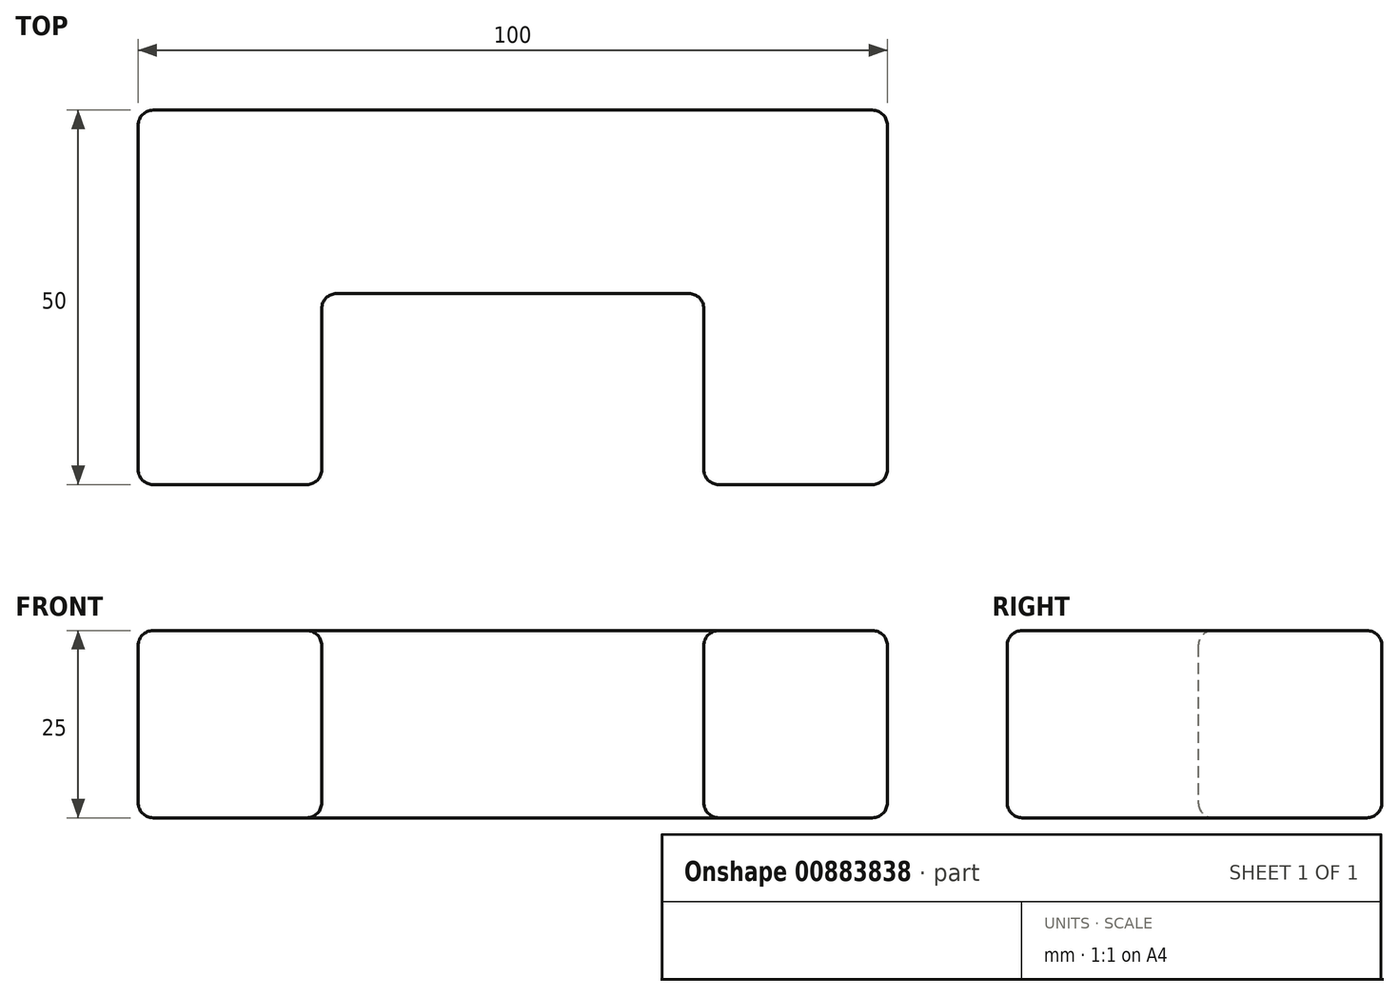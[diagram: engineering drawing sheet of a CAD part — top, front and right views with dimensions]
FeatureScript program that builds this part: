
annotation { "Feature Type Name" : "Feature", "Feature Type Description" : "" }
export const myFeature = defineFeature(function(context is Context, id is Id, definition is map)
    precondition{}
    {
        {
            var Q0;
            Q0=qCreatedBy(makeId("Top.planeOp"),FACE);
            var sketch = newSketch(context, id + "F0", { "sketchPlane" : qUnion([Q0])});
            skLineSegment(sketch, "E0", {"start": v(-50, 0) * mm, "end": v(-50, 50) * mm});
            skLineSegment(sketch, "E1", {"start": v(-50, 0) * mm, "end": v(-25.5, 0) * mm});
            skLineSegment(sketch, "E2", {"start": v(-25.5, 0) * mm, "end": v(-25.5, 25.5) * mm});
            skLineSegment(sketch, "E3.MirrorCS", {"start": v(25.5, 0) * mm, "end": v(25.5, 25.5) * mm});
            skLineSegment(sketch, "E4.MirrorCS", {"start": v(50, 0) * mm, "end": v(25.5, 0) * mm});
            skLineSegment(sketch, "E5.MirrorCS", {"start": v(50, 0) * mm, "end": v(50, 50) * mm});
            skLineSegment(sketch, "E6", {"start": v(-50, 50) * mm, "end": v(50, 50) * mm});
            skLineSegment(sketch, "E7", {"start": v(-25.5, 25.5) * mm, "end": v(25.5, 25.5) * mm});
            skSolve(sketch);
        }
        {
            var Q0;
            Q0 = qSketchRegion(id + "F0", true);
            extrude(context, id + "F1", {"entities" : qUnion([Q0]), "depth" : 25 * mm, "offsetDistance" : 25 * mm});
        }
        {
            var Q0;
            Q0=makeQuery(id+"F1.opExtrude","SWEPT_EDGE",EDGE,{"disambiguationData":[OSD([sQuery(id+"F0.wireOp",EDGE,"E0"),sQuery(id+"F0.wireOp",EDGE,"E6")])]});
            var Q1;
            Q1=makeQuery(id+"F1.opExtrude","CAP_EDGE",EDGE,{"disambiguationData":[OSD([sQuery(id+"F0.wireOp",EDGE,"E7")])],"isStart":false});
            var Q2;
            Q2=makeQuery(id+"F1.opExtrude","SWEPT_EDGE",EDGE,{"disambiguationData":[OSD([sQuery(id+"F0.wireOp",EDGE,"E0"),sQuery(id+"F0.wireOp",EDGE,"E1")])]});
            var Q3;
            Q3=makeQuery(id+"F1.opExtrude","SWEPT_EDGE",EDGE,{"disambiguationData":[OSD([sQuery(id+"F0.wireOp",EDGE,"E4.MirrorCS"),sQuery(id+"F0.wireOp",EDGE,"E5.MirrorCS")])]});
            var Q4;
            Q4=makeQuery(id+"F1.opExtrude","CAP_EDGE",EDGE,{"disambiguationData":[OSD([sQuery(id+"F0.wireOp",EDGE,"E6")])],"isStart":false});
            var Q5;
            Q5=makeQuery(id+"F1.opExtrude","CAP_EDGE",EDGE,{"disambiguationData":[OSD([sQuery(id+"F0.wireOp",EDGE,"E4.MirrorCS")])],"isStart":true});
            var Q6;
            Q6=makeQuery(id+"F1.opExtrude","SWEPT_EDGE",EDGE,{"disambiguationData":[OSD([sQuery(id+"F0.wireOp",EDGE,"E3.MirrorCS"),sQuery(id+"F0.wireOp",EDGE,"E4.MirrorCS")])]});
            var Q7;
            Q7=makeQuery(id+"F1.opExtrude","CAP_EDGE",EDGE,{"disambiguationData":[OSD([sQuery(id+"F0.wireOp",EDGE,"E0")])],"isStart":false});
            var Q8;
            Q8=makeQuery(id+"F1.opExtrude","CAP_EDGE",EDGE,{"disambiguationData":[OSD([sQuery(id+"F0.wireOp",EDGE,"E1")])],"isStart":false});
            var Q9;
            Q9=makeQuery(id+"F1.opExtrude","CAP_EDGE",EDGE,{"disambiguationData":[OSD([sQuery(id+"F0.wireOp",EDGE,"E0")])],"isStart":true});
            var Q10;
            Q10=makeQuery(id+"F1.opExtrude","SWEPT_EDGE",EDGE,{"disambiguationData":[OSD([sQuery(id+"F0.wireOp",EDGE,"E3.MirrorCS"),sQuery(id+"F0.wireOp",EDGE,"E7")])]});
            var Q11;
            Q11=makeQuery(id+"F1.opExtrude","CAP_EDGE",EDGE,{"disambiguationData":[OSD([sQuery(id+"F0.wireOp",EDGE,"E1")])],"isStart":true});
            var Q12;
            Q12=makeQuery(id+"F1.opExtrude","CAP_EDGE",EDGE,{"disambiguationData":[OSD([sQuery(id+"F0.wireOp",EDGE,"E7")])],"isStart":true});
            var Q13;
            Q13=makeQuery(id+"F1.opExtrude","CAP_EDGE",EDGE,{"disambiguationData":[OSD([sQuery(id+"F0.wireOp",EDGE,"E4.MirrorCS")])],"isStart":false});
            var Q14;
            Q14=makeQuery(id+"F1.opExtrude","CAP_EDGE",EDGE,{"disambiguationData":[OSD([sQuery(id+"F0.wireOp",EDGE,"E2")])],"isStart":false});
            var Q15;
            Q15=makeQuery(id+"F1.opExtrude","SWEPT_EDGE",EDGE,{"disambiguationData":[OSD([sQuery(id+"F0.wireOp",EDGE,"E2"),sQuery(id+"F0.wireOp",EDGE,"E7")])]});
            var Q16;
            Q16=makeQuery(id+"F1.opExtrude","CAP_EDGE",EDGE,{"disambiguationData":[OSD([sQuery(id+"F0.wireOp",EDGE,"E3.MirrorCS")])],"isStart":false});
            var Q17;
            Q17=makeQuery(id+"F1.opExtrude","SWEPT_EDGE",EDGE,{"disambiguationData":[OSD([sQuery(id+"F0.wireOp",EDGE,"E5.MirrorCS"),sQuery(id+"F0.wireOp",EDGE,"E6")])]});
            var Q18;
            Q18=makeQuery(id+"F1.opExtrude","CAP_EDGE",EDGE,{"disambiguationData":[OSD([sQuery(id+"F0.wireOp",EDGE,"E3.MirrorCS")])],"isStart":true});
            var Q19;
            Q19=makeQuery(id+"F1.opExtrude","CAP_EDGE",EDGE,{"disambiguationData":[OSD([sQuery(id+"F0.wireOp",EDGE,"E6")])],"isStart":true});
            var Q20;
            Q20=makeQuery(id+"F1.opExtrude","CAP_EDGE",EDGE,{"disambiguationData":[OSD([sQuery(id+"F0.wireOp",EDGE,"E5.MirrorCS")])],"isStart":false});
            var Q21;
            Q21=makeQuery(id+"F1.opExtrude","CAP_EDGE",EDGE,{"disambiguationData":[OSD([sQuery(id+"F0.wireOp",EDGE,"E5.MirrorCS")])],"isStart":true});
            var Q22;
            Q22=makeQuery(id+"F1.opExtrude","SWEPT_EDGE",EDGE,{"disambiguationData":[OSD([sQuery(id+"F0.wireOp",EDGE,"E1"),sQuery(id+"F0.wireOp",EDGE,"E2")])]});
            var Q23;
            Q23=makeQuery(id+"F1.opExtrude","CAP_EDGE",EDGE,{"disambiguationData":[OSD([sQuery(id+"F0.wireOp",EDGE,"E2")])],"isStart":true});
            fillet(context, id + "F2", {"entities" : qUnion([Q0, Q1, Q2, Q3, Q4, Q5, Q6, Q7, Q8, Q9, Q10, Q11, Q12, Q13, Q14, Q15, Q16, Q17, Q18, Q19, Q20, Q21, Q22, Q23]), "radius" : 2 * mm, "tangentPropagation" : true, "allowEdgeOverflow" : false});
        }
    });
